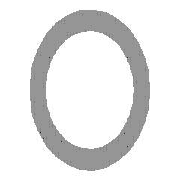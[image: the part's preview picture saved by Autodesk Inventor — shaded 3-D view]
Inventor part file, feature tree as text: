
AUTODESK INVENTOR PART (.ipt)
format: ipt  version: 2013 (Build 170138000, 138)  size: 116,736 bytes
history: native  units: mm (DEFAULTED — no unit token found)
features: other x4, sketch x3, plane x2, split x1
ambient origin geometry x8: Origin, YZ Plane, XZ Plane, XY Plane, X Axis, Y Axis, Z Axis, Center Point
bodies: Solid1 (feature_tree), Body (feature_tree)
feature tree (10):
  parser-record x1  (decoder bookkeeping rows leaked as tree rows — omitted from the tree; the rows remain in map.json)
  other  "Driven Length"
  other  "Start plane"
  other  "End plane"
  plane  "Work Plane4"
  split  "Split1"
  sketch  "Sketch"  dims[d2=131.474886mm d3=0.0mm d4=-0.0mm d5=131.474886mm d6=90.0deg d7=131.474886mm]
  sketch  "Sketch3"  dims[d0=33.401mm]
  plane  "Work Plane3"
  sketch  "Sketch4"  dims[d1=3.3782mm]
